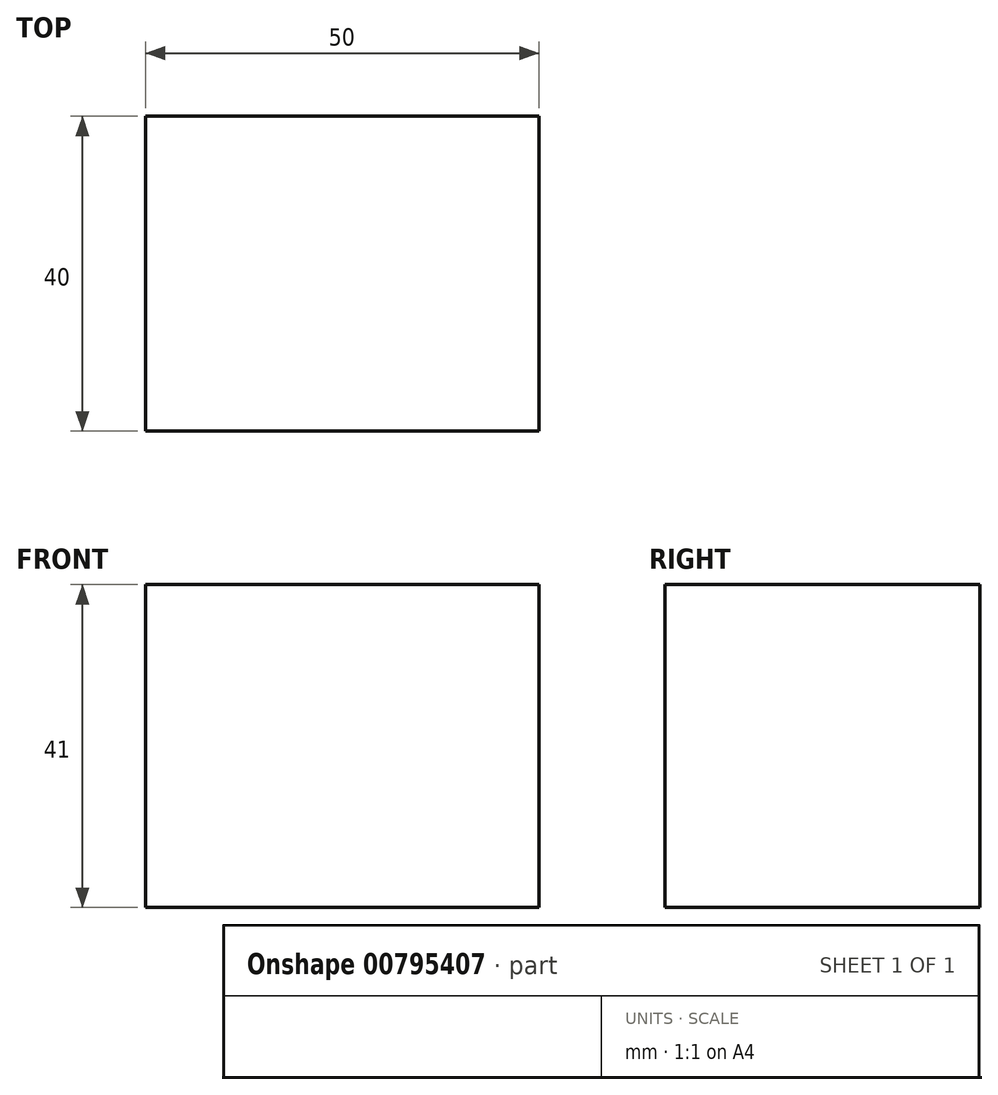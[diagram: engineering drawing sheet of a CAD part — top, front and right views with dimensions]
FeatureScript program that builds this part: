
annotation { "Feature Type Name" : "Feature", "Feature Type Description" : "" }
export const myFeature = defineFeature(function(context is Context, id is Id, definition is map)
    precondition{}
    {
        {
            var Q0;
            Q0=qCreatedBy(makeId("Top.planeOp"),FACE);
            var sketch = newSketch(context, id + "F0", { "sketchPlane" : qUnion([Q0])});
            skLineSegment(sketch, "E0.bottom", {"start": v(25, 20) * mm, "end": v(-25, 20) * mm});
            skLineSegment(sketch, "E0.top", {"start": v(25, -20) * mm, "end": v(-25, -20) * mm});
            skLineSegment(sketch, "E0.left", {"start": v(25, 20) * mm, "end": v(25, -20) * mm});
            skLineSegment(sketch, "E0.right", {"start": v(-25, 20) * mm, "end": v(-25, -20) * mm});
            skPoint(sketch, "E0.middle", {"position": v(0, 0) * mm});
            skSolve(sketch);
        }
        {
            var Q0;
            Q0 = qSketchRegion(id + "F0", true);
            extrude(context, id + "F1", {"entities" : qUnion([Q0]), "depth" : 41 * mm, "offsetDistance" : 25 * mm});
        }
    });
